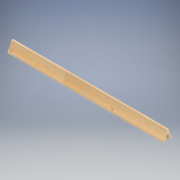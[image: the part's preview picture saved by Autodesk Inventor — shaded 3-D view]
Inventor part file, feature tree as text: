
AUTODESK INVENTOR PART (.ipt)
format: ipt  version: 2022.2 (Build 262287010, 287A)  size: 186,368 bytes
history: native  units: in
note: dims shown in document units (in); Inventor stores cm internally (conversion verified against a paired STEP export)
features: other x1, direct_edit x1, extrude x1, sketch x1, projected_geometry x1, revolve x1
ambient origin geometry x8: Origin, YZ Plane, XZ Plane, XY Plane, X Axis, Y Axis, Z Axis, Center Point
bodies: Solid1 (feature_tree)
feature tree (6):
  other  "North (1)"
  direct_edit  "Direct Edit1"
  extrude  "Extrusion1"  Depth=0.0625in TaperAngle=0.0deg
  sketch  "Sketch1"  dims[d0=-0.6184in d1=0.0625in d2=0.0in]
  projected_geometry  "Projected Loop1"
  revolve  "Rotate1"  [1 undecoded]
note: 1 required parameter value undecoded (feature->parameter linkage not recoverable at this tier; creation-order binding heuristic only, values carry confidence <= 0.55)
